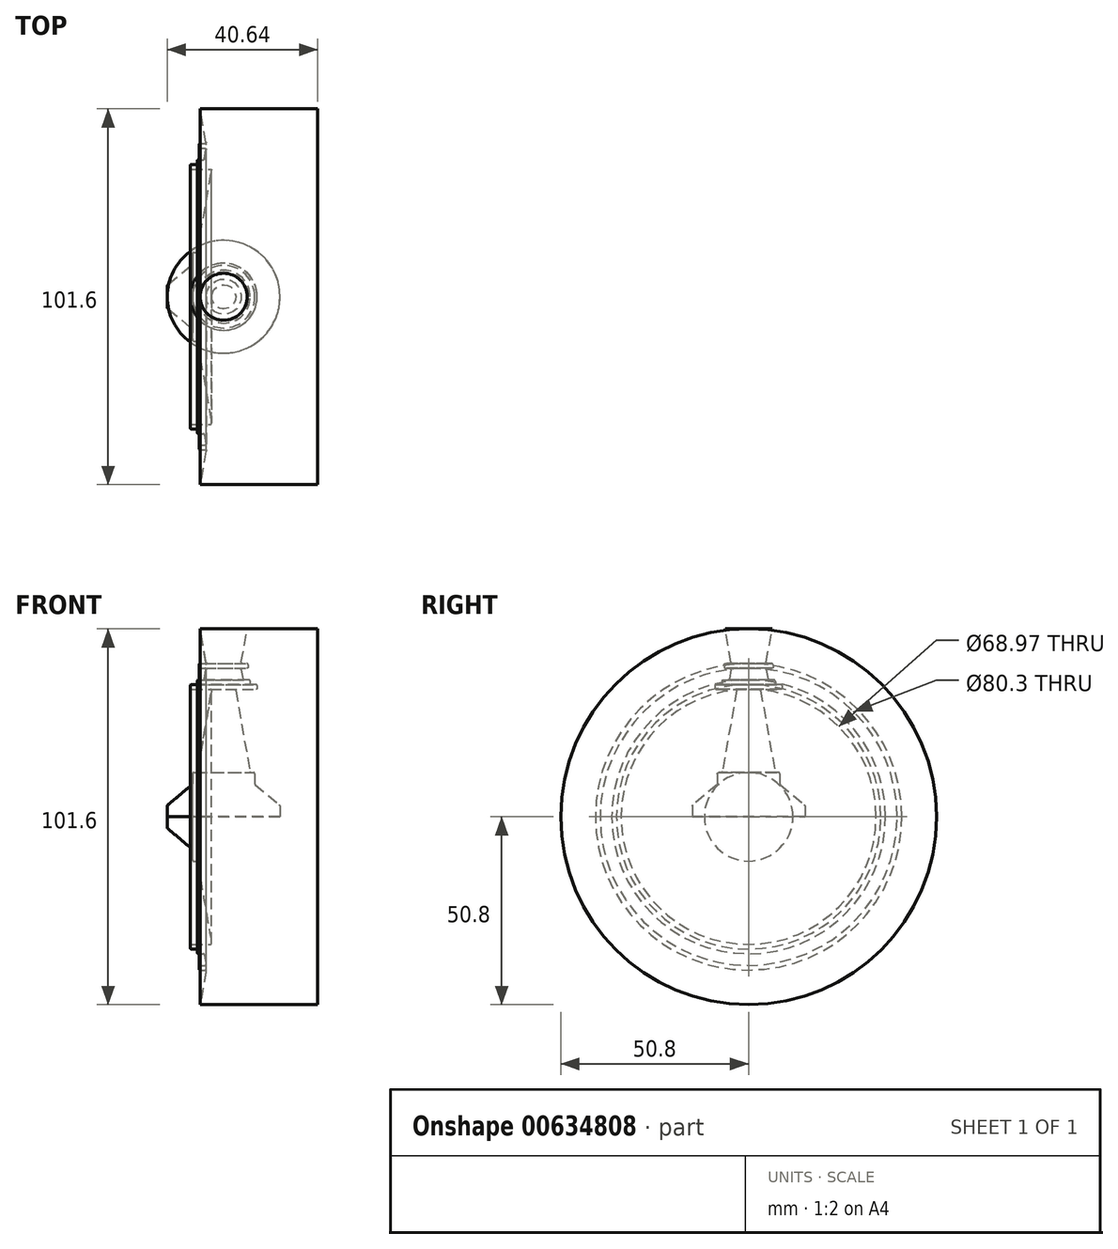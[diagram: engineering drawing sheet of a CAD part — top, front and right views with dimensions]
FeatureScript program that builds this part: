
annotation { "Feature Type Name" : "Feature", "Feature Type Description" : "" }
export const myFeature = defineFeature(function(context is Context, id is Id, definition is map)
    precondition{}
    {
        {
            var Q0;
            Q0=qCreatedBy(makeId("Front.planeOp"),FACE);
            var sketch = newSketch(context, id + "F0", { "sketchPlane" : qUnion([Q0])});
            skLineSegment(sketch, "E0.bottom", {"start": v(0, 0) * mm, "end": v(-15.24, 0) * mm});
            skLineSegment(sketch, "E0.top", {"start": v(0, 50.8) * mm, "end": v(-6.35, 50.8) * mm});
            skLineSegment(sketch, "E0.left", {"start": v(0, 0) * mm, "end": v(0, 50.8) * mm});
            skLineSegment(sketch, "E1", {"start": v(-15.24, 0) * mm, "end": v(-15.24, 2.93) * mm});
            skLineSegment(sketch, "E2", {"start": v(-15.13, 3.18) * mm, "end": v(-8.54, 8.7) * mm});
            skLineSegment(sketch, "E3", {"start": v(-8.43, 8.94) * mm, "end": v(-8.43, 11.65) * mm});
            skLineSegment(sketch, "E4", {"start": v(-8.11, 11.97) * mm, "end": v(-7.43, 11.97) * mm});
            skLineSegment(sketch, "E5", {"start": v(-7.11, 12.23) * mm, "end": v(-3.26, 34.11) * mm});
            skLineSegment(sketch, "E6", {"start": v(-3.57, 34.48) * mm, "end": v(-8.74, 34.48) * mm});
            skLineSegment(sketch, "E7", {"start": v(-9.06, 34.8) * mm, "end": v(-9.06, 35.44) * mm});
            skLineSegment(sketch, "E8", {"start": v(-8.74, 35.75) * mm, "end": v(-7.47, 35.75) * mm});
            skLineSegment(sketch, "E9", {"start": v(-7.15, 36.07) * mm, "end": v(-7.15, 36.7) * mm});
            skLineSegment(sketch, "E10", {"start": v(-6.83, 37.02) * mm, "end": v(-5.51, 37.02) * mm});
            skLineSegment(sketch, "E11", {"start": v(-5.2, 37.29) * mm, "end": v(-4.76, 39.78) * mm});
            skLineSegment(sketch, "E12", {"start": v(-5.07, 40.15) * mm, "end": v(-6.28, 40.15) * mm});
            skLineSegment(sketch, "E13", {"start": v(-6.6, 40.47) * mm, "end": v(-6.6, 41.1) * mm});
            skLineSegment(sketch, "E14", {"start": v(-6.28, 41.42) * mm, "end": v(-5.07, 41.42) * mm});
            skLineSegment(sketch, "E15", {"start": v(-4.76, 41.8) * mm, "end": v(-6.35, 50.8) * mm});
            skPoint(sketch, "E16.visualSharp", {"position": v(-15.24, 3.08) * mm});
            skArc(sketch, "E16.filletArc", {"start": v(-15.13, 3.18) * mm, "mid": v(-15.21, 3.07) * mm, "end": v(-15.24, 2.93) * mm});
            skPoint(sketch, "E17.visualSharp", {"position": v(-8.43, 8.8) * mm});
            skArc(sketch, "E17.filletArc", {"start": v(-8.54, 8.7) * mm, "mid": v(-8.46, 8.8) * mm, "end": v(-8.43, 8.94) * mm});
            skPoint(sketch, "E18.visualSharp", {"position": v(-3.2, 34.48) * mm});
            skArc(sketch, "E18.filletArc", {"start": v(-3.26, 34.11) * mm, "mid": v(-3.33, 34.37) * mm, "end": v(-3.57, 34.48) * mm});
            skPoint(sketch, "E19.visualSharp", {"position": v(-8.43, 11.97) * mm});
            skArc(sketch, "E19.filletArc", {"start": v(-8.11, 11.97) * mm, "mid": v(-8.34, 11.88) * mm, "end": v(-8.43, 11.65) * mm});
            skPoint(sketch, "E20.visualSharp", {"position": v(-7.16, 11.97) * mm});
            skArc(sketch, "E20.filletArc", {"start": v(-7.43, 11.97) * mm, "mid": v(-7.22, 12.04) * mm, "end": v(-7.11, 12.23) * mm});
            skPoint(sketch, "E21.visualSharp", {"position": v(-9.06, 34.48) * mm});
            skArc(sketch, "E21.filletArc", {"start": v(-9.06, 34.8) * mm, "mid": v(-8.96, 34.58) * mm, "end": v(-8.74, 34.48) * mm});
            skPoint(sketch, "E22.visualSharp", {"position": v(-9.06, 35.75) * mm});
            skArc(sketch, "E22.filletArc", {"start": v(-8.74, 35.75) * mm, "mid": v(-8.96, 35.66) * mm, "end": v(-9.06, 35.44) * mm});
            skPoint(sketch, "E23.visualSharp", {"position": v(-7.15, 35.75) * mm});
            skArc(sketch, "E23.filletArc", {"start": v(-7.47, 35.75) * mm, "mid": v(-7.25, 35.85) * mm, "end": v(-7.15, 36.07) * mm});
            skPoint(sketch, "E24.visualSharp", {"position": v(-7.15, 37.02) * mm});
            skArc(sketch, "E24.filletArc", {"start": v(-6.83, 37.02) * mm, "mid": v(-7.06, 36.93) * mm, "end": v(-7.15, 36.7) * mm});
            skPoint(sketch, "E25.visualSharp", {"position": v(-5.25, 37.02) * mm});
            skArc(sketch, "E25.filletArc", {"start": v(-5.51, 37.02) * mm, "mid": v(-5.3, 37.1) * mm, "end": v(-5.2, 37.29) * mm});
            skPoint(sketch, "E26.visualSharp", {"position": v(-4.7, 40.15) * mm});
            skArc(sketch, "E26.filletArc", {"start": v(-4.76, 39.78) * mm, "mid": v(-4.83, 40.04) * mm, "end": v(-5.07, 40.15) * mm});
            skPoint(sketch, "E27.visualSharp", {"position": v(-6.6, 40.15) * mm});
            skArc(sketch, "E27.filletArc", {"start": v(-6.6, 40.47) * mm, "mid": v(-6.5, 40.24) * mm, "end": v(-6.28, 40.15) * mm});
            skPoint(sketch, "E28.visualSharp", {"position": v(-6.6, 41.42) * mm});
            skArc(sketch, "E28.filletArc", {"start": v(-6.28, 41.42) * mm, "mid": v(-6.5, 41.33) * mm, "end": v(-6.6, 41.1) * mm});
            skPoint(sketch, "E29.visualSharp", {"position": v(-4.7, 41.42) * mm});
            skArc(sketch, "E29.filletArc", {"start": v(-5.07, 41.42) * mm, "mid": v(-4.83, 41.53) * mm, "end": v(-4.76, 41.8) * mm});
            skSolve(sketch);
        }
        {
            var Q0;
            Q0=makeQuery(id+"F0.imprint","IMPRINT",FACE,{"disambiguationData":[TD([[makeQuery(id+"F0.imprint","IMPRINT",EDGE,{"derivedFrom":sQuery(id+"F0.wireOp",EDGE,"E0.bottom")}),-1.0]])]});
            var Q1;
            Q1=sQuery(id+"F0.wireOp",EDGE,"E0.bottom");
            revolve(context, id + "F1", {"entities" : qUnion([Q0]), "axis" : qUnion([Q1]), "revolveType" : RevolveType.FULL});
        }
        {
            var Q0;
            Q0=makeQuery(id+"F1.opRevolve","SWEPT_FACE",FACE,{"disambiguationData":[OSD([sQuery(id+"F0.wireOp",EDGE,"E0.left")])]});
            extrude(context, id + "F2", {"entities" : qUnion([Q0]), "operationType" : NewBodyOperationType.ADD, "depth" : 25.4 * mm, "offsetDistance" : 25.4 * mm});
        }
        {
            var Q0;
            Q0=makeQuery(id+"F0.imprint","IMPRINT",FACE,{"disambiguationData":[TD([[makeQuery(id+"F0.imprint","IMPRINT",EDGE,{"derivedFrom":sQuery(id+"F0.wireOp",EDGE,"E0.bottom")}),-1.0]])]});
            var Q1;
            Q1=sQuery(id+"F0.wireOp",EDGE,"E0.left");
            revolve(context, id + "F3", {"entities" : qUnion([Q0]), "axis" : qUnion([Q1]), "revolveType" : RevolveType.FULL});
        }
    });
